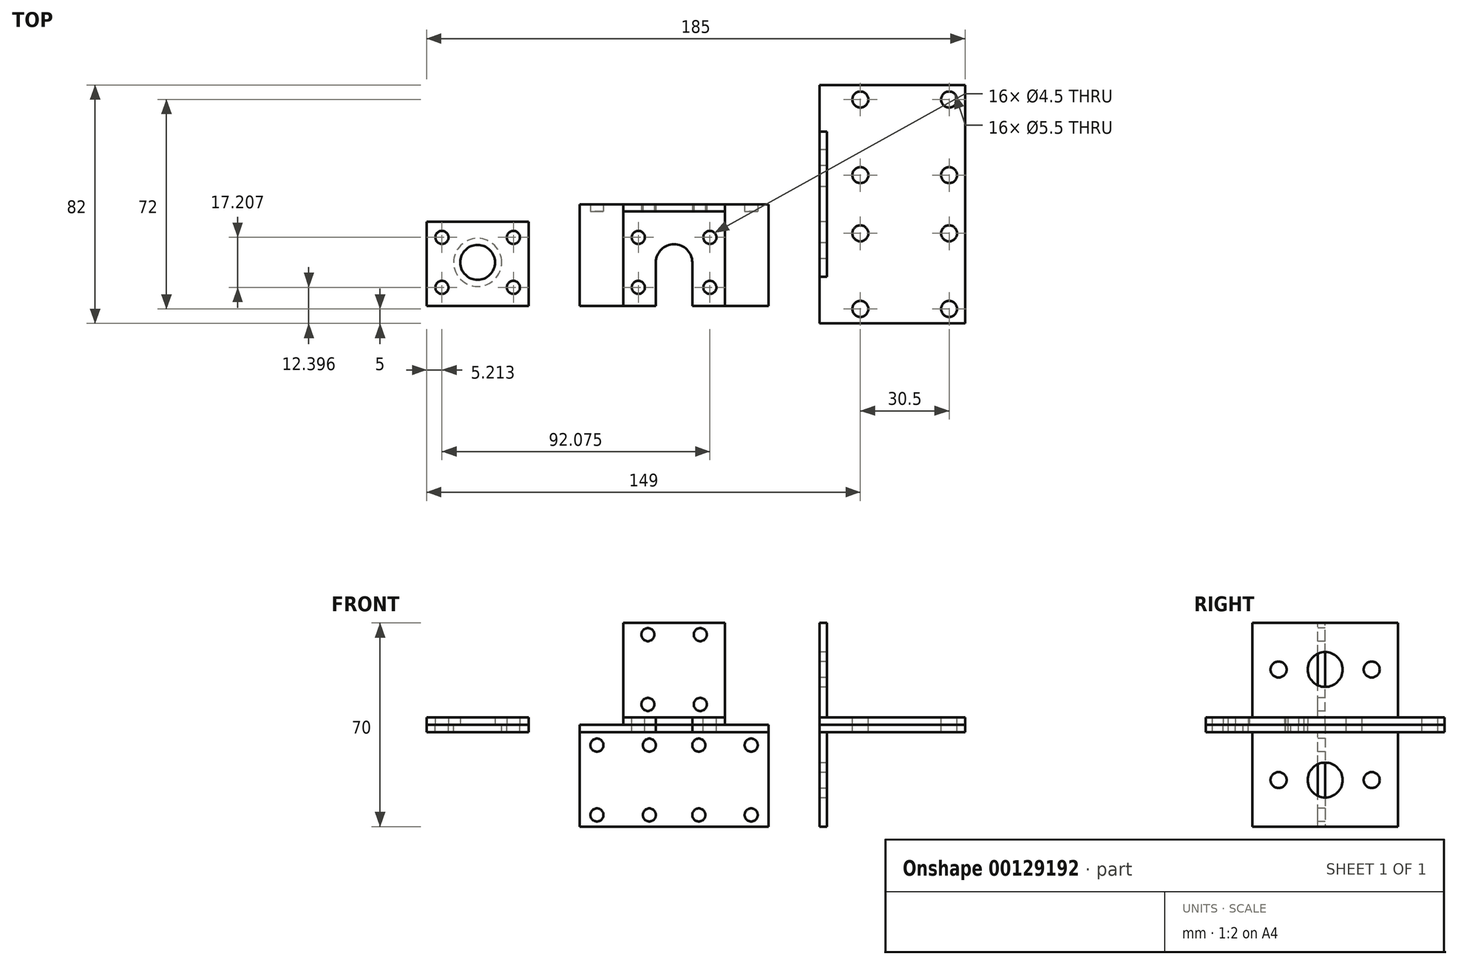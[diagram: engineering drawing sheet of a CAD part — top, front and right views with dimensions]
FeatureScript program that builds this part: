
annotation { "Feature Type Name" : "Feature", "Feature Type Description" : "" }
export const myFeature = defineFeature(function(context is Context, id is Id, definition is map)
    precondition{}
    {
        {
            var Q0;
            Q0=qCreatedBy(makeId("Right.planeOp"),FACE);
            cPlane(context, id + "F0", {"entities" : qUnion([Q0]), "cplaneType" : CPlaneType.OFFSET, "offset" : 50 * mm, "width" : 150 * mm, "height" : 150 * mm});
        }
        {
            var Q0;
            Q0=qCreatedBy(makeId("Right.planeOp"),FACE);
            var sketch = newSketch(context, id + "F1", { "sketchPlane" : qUnion([Q0])});
            skLineSegment(sketch, "E0.bottom", {"start": v(0, 0) * mm, "end": v(-35, 0) * mm});
            skLineSegment(sketch, "E0.top", {"start": v(0, 2.5) * mm, "end": v(-35, 2.5) * mm});
            skLineSegment(sketch, "E0.left", {"start": v(0, 0) * mm, "end": v(0, 2.5) * mm});
            skLineSegment(sketch, "E0.right", {"start": v(-35, 0) * mm, "end": v(-35, 2.5) * mm});
            skLineSegment(sketch, "E1.bottom", {"start": v(0, 2.5) * mm, "end": v(-2.5, 2.5) * mm});
            skLineSegment(sketch, "E1.top", {"start": v(0, 35) * mm, "end": v(-2.5, 35) * mm});
            skLineSegment(sketch, "E1.left", {"start": v(0, 2.5) * mm, "end": v(0, 35) * mm});
            skLineSegment(sketch, "E1.right", {"start": v(-2.5, 2.5) * mm, "end": v(-2.5, 35) * mm});
            skLineSegment(sketch, "E2.bottom", {"start": v(0, 0) * mm, "end": v(-2.5, 0) * mm});
            skLineSegment(sketch, "E2.right", {"start": v(-2.5, 0) * mm, "end": v(-2.5, 2.5) * mm});
            skSolve(sketch);
        }
        {
            var Q0;
            Q0=makeQuery(id+"F1.imprint","IMPRINT",FACE,{"disambiguationData":[TD([[makeQuery(id+"F1.imprint","IMPRINT",EDGE,{"derivedFrom":sQuery(id+"F1.wireOp",EDGE,"E0.bottom")}),-1.0]])]});
            var Q1;
            Q1=makeQuery(id+"F1.imprint","IMPRINT",FACE,{"disambiguationData":[TD([[makeQuery(id+"F1.imprint","IMPRINT",EDGE,{"derivedFrom":sQuery(id+"F1.wireOp",EDGE,"E2.bottom")}),-1.0]])]});
            extrude(context, id + "F2", {"entities" : qUnion([Q0, Q1]), "endBound" : BoundingType.SYMMETRIC, "depth" : 35 * mm});
        }
        {
            var Q0;
            Q0=makeQuery(id+"F1.imprint","IMPRINT",FACE,{"disambiguationData":[TD([[makeQuery(id+"F1.imprint","IMPRINT",EDGE,{"derivedFrom":sQuery(id+"F1.wireOp",EDGE,"E2.bottom")}),-1.0]])]});
            var Q1;
            Q1=makeQuery(id+"F1.imprint","IMPRINT",FACE,{"disambiguationData":[TD([[makeQuery(id+"F1.imprint","IMPRINT",EDGE,{"derivedFrom":sQuery(id+"F1.wireOp",EDGE,"E1.top")}),1.0]])]});
            extrude(context, id + "F3", {"entities" : qUnion([Q0, Q1]), "operationType" : NewBodyOperationType.ADD, "endBound" : BoundingType.SYMMETRIC, "depth" : 35 * mm});
        }
        {
            var Q0;
            Q0=qCreatedBy(makeId("Right.planeOp"),FACE);
            var sketch = newSketch(context, id + "F4", { "sketchPlane" : qUnion([Q0])});
            skLineSegment(sketch, "E3.bottom", {"start": v(0, -35) * mm, "end": v(-2.5, -35) * mm});
            skLineSegment(sketch, "E3.top", {"start": v(0, -2.5) * mm, "end": v(-2.5, -2.5) * mm});
            skLineSegment(sketch, "E3.left", {"start": v(0, -35) * mm, "end": v(0, -2.5) * mm});
            skLineSegment(sketch, "E3.right", {"start": v(-2.5, -35) * mm, "end": v(-2.5, -2.5) * mm});
            skLineSegment(sketch, "E4.bottom", {"start": v(0, 0) * mm, "end": v(-35, 0) * mm});
            skLineSegment(sketch, "E4.top", {"start": v(0, -2.5) * mm, "end": v(-35, -2.5) * mm});
            skLineSegment(sketch, "E4.left", {"start": v(0, 0) * mm, "end": v(0, -2.5) * mm});
            skLineSegment(sketch, "E4.right", {"start": v(-35, 0) * mm, "end": v(-35, -2.5) * mm});
            skLineSegment(sketch, "E5.bottom", {"start": v(-2.5, -2.5) * mm, "end": v(0, -2.5) * mm});
            skLineSegment(sketch, "E5.top", {"start": v(-2.5, 0) * mm, "end": v(0, 0) * mm});
            skLineSegment(sketch, "E5.left", {"start": v(-2.5, -2.5) * mm, "end": v(-2.5, 0) * mm});
            skLineSegment(sketch, "E5.right", {"start": v(0, -2.5) * mm, "end": v(0, 0) * mm});
            skSolve(sketch);
        }
        {
            var Q0;
            Q0=makeQuery(id+"F4.imprint","IMPRINT",FACE,{"disambiguationData":[TD([[makeQuery(id+"F4.imprint","IMPRINT",EDGE,{"derivedFrom":sQuery(id+"F4.wireOp",EDGE,"E4.bottom")}),1.0]])]});
            var Q1;
            Q1=makeQuery(id+"F4.imprint","IMPRINT",FACE,{"disambiguationData":[TD([[makeQuery(id+"F4.imprint","IMPRINT",EDGE,{"derivedFrom":sQuery(id+"F4.wireOp",EDGE,"E5.bottom")}),1.0]])]});
            extrude(context, id + "F5", {"entities" : qUnion([Q0, Q1]), "endBound" : BoundingType.SYMMETRIC, "depth" : 65 * mm});
        }
        {
            var Q0;
            Q0=makeQuery(id+"F4.imprint","IMPRINT",FACE,{"disambiguationData":[TD([[makeQuery(id+"F4.imprint","IMPRINT",EDGE,{"derivedFrom":sQuery(id+"F4.wireOp",EDGE,"E3.bottom")}),-1.0]])]});
            var Q1;
            Q1=makeQuery(id+"F4.imprint","IMPRINT",FACE,{"disambiguationData":[TD([[makeQuery(id+"F4.imprint","IMPRINT",EDGE,{"derivedFrom":sQuery(id+"F4.wireOp",EDGE,"E5.bottom")}),1.0]])]});
            extrude(context, id + "F6", {"entities" : qUnion([Q0, Q1]), "operationType" : NewBodyOperationType.ADD, "endBound" : BoundingType.SYMMETRIC, "depth" : 65 * mm});
        }
        {
            var Q0;
            Q0=qCreatedBy(makeId("Front.planeOp"),FACE);
            var sketch = newSketch(context, id + "F7", { "sketchPlane" : qUnion([Q0])});
            skLineSegment(sketch, "E6", {"start": v(78.4, 7) * mm, "end": v(-89.42, 7) * mm, "construction": true});
            skLineSegment(sketch, "E7", {"start": v(80.33, -7) * mm, "end": v(-90.65, -7) * mm, "construction": true});
            skLineSegment(sketch, "E8", {"start": v(62.65, 7) * mm, "end": v(62.65, 0) * mm, "construction": true});
            skLineSegment(sketch, "E9", {"start": v(62.65, 0) * mm, "end": v(62.65, -7) * mm, "construction": true});
            skCircle(sketch, "E10", {"center": v(-26.5, -7) * mm, "radius": 2.25 * mm});
            skCircle(sketch, "E11", {"center": v(-8.5, -7) * mm, "radius": 2.25 * mm});
            skCircle(sketch, "E12", {"center": v(8.5, -7) * mm, "radius": 2.25 * mm});
            skCircle(sketch, "E13", {"center": v(26.5, -7) * mm, "radius": 2.25 * mm});
            skLineSegment(sketch, "E14", {"start": v(-38.38, -31) * mm, "end": v(47.7, -31) * mm, "construction": true});
            skCircle(sketch, "E15", {"center": v(-26.5, -31) * mm, "radius": 2.25 * mm});
            skCircle(sketch, "E16", {"center": v(-8.5, -31) * mm, "radius": 2.25 * mm});
            skCircle(sketch, "E17", {"center": v(8.5, -31) * mm, "radius": 2.25 * mm});
            skCircle(sketch, "E18", {"center": v(26.5, -31) * mm, "radius": 2.25 * mm});
            skLineSegment(sketch, "E19", {"start": v(0, 52.5) * mm, "end": v(0, -66.42) * mm, "construction": true});
            skLineSegment(sketch, "E20", {"start": v(26.5, -5.99) * mm, "end": v(26.5, -56.02) * mm, "construction": true});
            skLineSegment(sketch, "E21", {"start": v(8.5, -5.9) * mm, "end": v(8.5, -56.8) * mm, "construction": true});
            skLineSegment(sketch, "E22", {"start": v(-8.5, -56.8) * mm, "end": v(-8.5, -6.69) * mm, "construction": true});
            skLineSegment(sketch, "E23", {"start": v(-26.5, -6.69) * mm, "end": v(-26.5, -58.57) * mm, "construction": true});
            skLineSegment(sketch, "E24", {"start": v(3.5, -5.72) * mm, "end": v(3.5, -57.57) * mm, "construction": true});
            skLineSegment(sketch, "E25", {"start": v(-3.5, -57.57) * mm, "end": v(-3.5, -6.02) * mm, "construction": true});
            skLineSegment(sketch, "E26", {"start": v(0, -48.24) * mm, "end": v(3.5, -48.24) * mm, "construction": true});
            skLineSegment(sketch, "E27", {"start": v(0, -48.24) * mm, "end": v(-3.5, -48.24) * mm, "construction": true});
            skLineSegment(sketch, "E28", {"start": v(8.5, -53.82) * mm, "end": v(3.5, -53.82) * mm, "construction": true});
            skLineSegment(sketch, "E29", {"start": v(-3.5, -54.17) * mm, "end": v(-8.5, -54.17) * mm, "construction": true});
            skLineSegment(sketch, "E30", {"start": v(46.98, 31) * mm, "end": v(-43.4, 31) * mm, "construction": true});
            skLineSegment(sketch, "E31", {"start": v(9, 3.25) * mm, "end": v(9, 53.28) * mm, "construction": true});
            skLineSegment(sketch, "E32", {"start": v(-9, 4.66) * mm, "end": v(-9, 53.81) * mm, "construction": true});
            skLineSegment(sketch, "E33", {"start": v(9, 48) * mm, "end": v(0, 48) * mm, "construction": true});
            skLineSegment(sketch, "E34", {"start": v(0, 48) * mm, "end": v(-9, 48) * mm, "construction": true});
            skCircle(sketch, "E35", {"center": v(9, 31) * mm, "radius": 2.25 * mm});
            skCircle(sketch, "E36", {"center": v(9, 7) * mm, "radius": 2.25 * mm});
            skCircle(sketch, "E37", {"center": v(-9, 7) * mm, "radius": 2.25 * mm});
            skCircle(sketch, "E38", {"center": v(-9, 31) * mm, "radius": 2.25 * mm});
            skSolve(sketch);
        }
        {
            var Q0;
            Q0=makeQuery(id+"F7.imprint","IMPRINT",FACE,{"disambiguationData":[TD([[makeQuery(id+"F7.imprint","IMPRINT",EDGE,{"derivedFrom":sQuery(id+"F7.wireOp",EDGE,"E35")}),1.0]])]});
            var Q1;
            Q1=makeQuery(id+"F7.imprint","IMPRINT",FACE,{"disambiguationData":[TD([[makeQuery(id+"F7.imprint","IMPRINT",EDGE,{"derivedFrom":sQuery(id+"F7.wireOp",EDGE,"E36")}),1.0]])]});
            var Q2;
            Q2=makeQuery(id+"F7.imprint","IMPRINT",FACE,{"disambiguationData":[TD([[makeQuery(id+"F7.imprint","IMPRINT",EDGE,{"derivedFrom":sQuery(id+"F7.wireOp",EDGE,"E37")}),1.0]])]});
            var Q3;
            Q3=makeQuery(id+"F7.imprint","IMPRINT",FACE,{"disambiguationData":[TD([[makeQuery(id+"F7.imprint","IMPRINT",EDGE,{"derivedFrom":sQuery(id+"F7.wireOp",EDGE,"E38")}),1.0]])]});
            extrude(context, id + "F8", {"entities" : qUnion([Q0, Q1, Q2, Q3]), "operationType" : NewBodyOperationType.REMOVE, "endBound" : BoundingType.SYMMETRIC, "oppositeDirection" : true, "depth" : 10 * mm});
        }
        {
            var Q0;
            Q0=makeQuery(id+"F7.imprint","IMPRINT",FACE,{"disambiguationData":[TD([[makeQuery(id+"F7.imprint","IMPRINT",EDGE,{"derivedFrom":sQuery(id+"F7.wireOp",EDGE,"E13")}),1.0]])]});
            var Q1;
            Q1=makeQuery(id+"F7.imprint","IMPRINT",FACE,{"disambiguationData":[TD([[makeQuery(id+"F7.imprint","IMPRINT",EDGE,{"derivedFrom":sQuery(id+"F7.wireOp",EDGE,"E12")}),1.0]])]});
            var Q2;
            Q2=makeQuery(id+"F7.imprint","IMPRINT",FACE,{"disambiguationData":[TD([[makeQuery(id+"F7.imprint","IMPRINT",EDGE,{"derivedFrom":sQuery(id+"F7.wireOp",EDGE,"E11")}),1.0]])]});
            var Q3;
            Q3=makeQuery(id+"F7.imprint","IMPRINT",FACE,{"disambiguationData":[TD([[makeQuery(id+"F7.imprint","IMPRINT",EDGE,{"derivedFrom":sQuery(id+"F7.wireOp",EDGE,"E10")}),1.0]])]});
            var Q4;
            Q4=makeQuery(id+"F7.imprint","IMPRINT",FACE,{"disambiguationData":[TD([[makeQuery(id+"F7.imprint","IMPRINT",EDGE,{"derivedFrom":sQuery(id+"F7.wireOp",EDGE,"E15")}),1.0]])]});
            var Q5;
            Q5=makeQuery(id+"F7.imprint","IMPRINT",FACE,{"disambiguationData":[TD([[makeQuery(id+"F7.imprint","IMPRINT",EDGE,{"derivedFrom":sQuery(id+"F7.wireOp",EDGE,"E16")}),1.0]])]});
            var Q6;
            Q6=makeQuery(id+"F7.imprint","IMPRINT",FACE,{"disambiguationData":[TD([[makeQuery(id+"F7.imprint","IMPRINT",EDGE,{"derivedFrom":sQuery(id+"F7.wireOp",EDGE,"E17")}),1.0]])]});
            var Q7;
            Q7=makeQuery(id+"F7.imprint","IMPRINT",FACE,{"disambiguationData":[TD([[makeQuery(id+"F7.imprint","IMPRINT",EDGE,{"derivedFrom":sQuery(id+"F7.wireOp",EDGE,"E18")}),1.0]])]});
            extrude(context, id + "F9", {"entities" : qUnion([Q0, Q1, Q2, Q3, Q4, Q5, Q6, Q7]), "operationType" : NewBodyOperationType.REMOVE, "endBound" : BoundingType.SYMMETRIC, "oppositeDirection" : true, "depth" : 10 * mm});
        }
        {
            var Q0;
            Q0=qCreatedBy(makeId("Top.planeOp"),FACE);
            var sketch = newSketch(context, id + "F10", { "sketchPlane" : qUnion([Q0])});
            skLineSegment(sketch, "E39.bottom", {"start": v(-85, -6) * mm, "end": v(-50, -6) * mm});
            skLineSegment(sketch, "E39.top", {"start": v(-85, -35) * mm, "end": v(-50, -35) * mm});
            skLineSegment(sketch, "E39.left", {"start": v(-85, -35) * mm, "end": v(-85, -6) * mm});
            skLineSegment(sketch, "E39.right", {"start": v(-50, -35) * mm, "end": v(-50, -6) * mm});
            skLineSegment(sketch, "E40", {"start": v(-85, -20) * mm, "end": v(-67.5, -20) * mm, "construction": true});
            skLineSegment(sketch, "E41", {"start": v(-67.5, -20) * mm, "end": v(-50, -20) * mm, "construction": true});
            skLineSegment(sketch, "E42", {"start": v(-67.5, -35) * mm, "end": v(-67.5, -20) * mm, "construction": true});
            skCircle(sketch, "E43", {"center": v(-67.5, -20) * mm, "radius": 8.25 * mm});
            skCircle(sketch, "E44", {"center": v(-79.79, -28.6) * mm, "radius": 2.25 * mm});
            skLineSegment(sketch, "E45", {"start": v(-67.5, -20) * mm, "end": v(-55.21, -11.4) * mm, "construction": true});
            skLineSegment(sketch, "E46", {"start": v(-79.79, -28.6) * mm, "end": v(-67.5, -20) * mm});
            skCircle(sketch, "E47", {"center": v(-55.21, -11.4) * mm, "radius": 2.25 * mm});
            skCircle(sketch, "E48", {"center": v(-79.79, -11.4) * mm, "radius": 2.25 * mm});
            skLineSegment(sketch, "E49", {"start": v(-67.5, -20) * mm, "end": v(-79.79, -11.4) * mm, "construction": true});
            skCircle(sketch, "E50", {"center": v(-55.21, -28.6) * mm, "radius": 2.25 * mm});
            skLineSegment(sketch, "E51", {"start": v(-67.5, -20) * mm, "end": v(-55.21, -28.6) * mm, "construction": true});
            skCircle(sketch, "E52", {"center": v(-67.5, -20) * mm, "radius": 6 * mm});
            skLineSegment(sketch, "E53", {"start": v(-37.49, -20) * mm, "end": v(-99.92, -20) * mm, "construction": true});
            skSolve(sketch);
        }
        {
            var Q0;
            Q0=qCreatedBy(makeId("Top.planeOp"),FACE);
            var sketch = newSketch(context, id + "F11", { "sketchPlane" : qUnion([Q0])});
            skLineSegment(sketch, "E54", {"start": v(0, 16.43) * mm, "end": v(0, -56.43) * mm, "construction": true});
            skLineSegment(sketch, "E55", {"start": v(-39.4, -20) * mm, "end": v(51.73, -20) * mm, "construction": true});
            skPoint(sketch, "E55.endSnap0", {"position": v(0, -20) * mm});
            skCircle(sketch, "E56", {"center": v(0, -20) * mm, "radius": 6.25 * mm});
            skLineSegment(sketch, "E57", {"start": v(-6.25, -20) * mm, "end": v(-6.25, -44.93) * mm});
            skLineSegment(sketch, "E58", {"start": v(-6.25, -44.93) * mm, "end": v(6.25, -44.93) * mm});
            skLineSegment(sketch, "E59", {"start": v(6.25, -44.93) * mm, "end": v(6.25, -20) * mm});
            skLineSegment(sketch, "E60", {"start": v(0, -20) * mm, "end": v(12.29, -11.4) * mm, "construction": true});
            skLineSegment(sketch, "E61", {"start": v(0, -20) * mm, "end": v(-12.29, -11.4) * mm, "construction": true});
            skLineSegment(sketch, "E62", {"start": v(0, -20) * mm, "end": v(-12.29, -28.6) * mm, "construction": true});
            skLineSegment(sketch, "E63", {"start": v(0, -20) * mm, "end": v(12.29, -28.6) * mm, "construction": true});
            skCircle(sketch, "E64", {"center": v(-12.29, -11.4) * mm, "radius": 2.25 * mm});
            skCircle(sketch, "E65", {"center": v(12.29, -11.4) * mm, "radius": 2.25 * mm});
            skCircle(sketch, "E66", {"center": v(12.29, -28.6) * mm, "radius": 2.25 * mm});
            skCircle(sketch, "E67", {"center": v(-12.29, -28.6) * mm, "radius": 2.25 * mm});
            skSolve(sketch);
        }
        {
            var Q0;
            Q0=makeQuery(id+"F11.imprint","IMPRINT",FACE,{"disambiguationData":[TD([[makeQuery(id+"F11.imprint","IMPRINT",EDGE,{"derivedFrom":sQuery(id+"F11.wireOp",EDGE,"E56")}),1.0]])]});
            var Q1;
            {var subQ0=sQuery(id+"F11.wireOp",EDGE,"E57");Q1=makeQuery(id+"F11.imprint","IMPRINT",FACE,{"disambiguationData":[TD([[makeQuery(id+"F11.imprint","IMPRINT",EDGE,{"derivedFrom":subQ0}),1.0]])]});}
            var Q2;
            Q2=makeQuery(id+"F11.imprint","IMPRINT",FACE,{"disambiguationData":[TD([[makeQuery(id+"F11.imprint","IMPRINT",EDGE,{"derivedFrom":sQuery(id+"F11.wireOp",EDGE,"E64")}),1.0]])]});
            var Q3;
            Q3=makeQuery(id+"F11.imprint","IMPRINT",FACE,{"disambiguationData":[TD([[makeQuery(id+"F11.imprint","IMPRINT",EDGE,{"derivedFrom":sQuery(id+"F11.wireOp",EDGE,"E65")}),1.0]])]});
            var Q4;
            Q4=makeQuery(id+"F11.imprint","IMPRINT",FACE,{"disambiguationData":[TD([[makeQuery(id+"F11.imprint","IMPRINT",EDGE,{"derivedFrom":sQuery(id+"F11.wireOp",EDGE,"E66")}),1.0]])]});
            var Q5;
            Q5=makeQuery(id+"F11.imprint","IMPRINT",FACE,{"disambiguationData":[TD([[makeQuery(id+"F11.imprint","IMPRINT",EDGE,{"derivedFrom":sQuery(id+"F11.wireOp",EDGE,"E67")}),1.0]])]});
            extrude(context, id + "F12", {"entities" : qUnion([Q0, Q1, Q2, Q3, Q4, Q5]), "operationType" : NewBodyOperationType.REMOVE, "endBound" : BoundingType.SYMMETRIC, "oppositeDirection" : true, "depth" : 10 * mm});
        }
        {
            var Q0;
            Q0=makeQuery(id+"F10.imprint","IMPRINT",FACE,{"disambiguationData":[TD([[makeQuery(id+"F10.imprint","IMPRINT",EDGE,{"derivedFrom":sQuery(id+"F10.wireOp",EDGE,"E39.bottom")}),-1.0]])]});
            extrude(context, id + "F13", {"entities" : qUnion([Q0]), "oppositeDirection" : true, "depth" : 2.5 * mm});
        }
        {
            var Q0;
            Q0=makeQuery(id+"F10.imprint","IMPRINT",FACE,{"disambiguationData":[TD([[makeQuery(id+"F10.imprint","IMPRINT",EDGE,{"derivedFrom":sQuery(id+"F10.wireOp",EDGE,"E39.bottom")}),-1.0]])]});
            var Q1;
            Q1=makeQuery(id+"F10.imprint","IMPRINT",FACE,{"disambiguationData":[TD([[makeQuery(id+"F10.imprint","IMPRINT",EDGE,{"derivedFrom":sQuery(id+"F10.wireOp",EDGE,"E43")}),1.0]])]});
            extrude(context, id + "F14", {"entities" : qUnion([Q0, Q1]), "depth" : 2.5 * mm});
        }
        {
            var Q0;
            Q0=qCreatedBy(makeId("Front.planeOp"),FACE);
            var sketch = newSketch(context, id + "F15", { "sketchPlane" : qUnion([Q0])});
            skLineSegment(sketch, "E68", {"start": v(50, 72.04) * mm, "end": v(50, -62.88) * mm, "construction": true});
            skLineSegment(sketch, "E69.bottom", {"start": v(50, 0) * mm, "end": v(100, 0) * mm});
            skLineSegment(sketch, "E69.top", {"start": v(50, -2.5) * mm, "end": v(100, -2.5) * mm});
            skLineSegment(sketch, "E69.left", {"start": v(50, 0) * mm, "end": v(50, -2.5) * mm});
            skLineSegment(sketch, "E69.right", {"start": v(100, 0) * mm, "end": v(100, -2.5) * mm});
            skLineSegment(sketch, "E70.bottom", {"start": v(50, -2.5) * mm, "end": v(52.5, -2.5) * mm});
            skLineSegment(sketch, "E70.top", {"start": v(50, -35) * mm, "end": v(52.5, -35) * mm});
            skLineSegment(sketch, "E70.left", {"start": v(50, -2.5) * mm, "end": v(50, -35) * mm});
            skLineSegment(sketch, "E70.right", {"start": v(52.5, -2.5) * mm, "end": v(52.5, -35) * mm});
            skLineSegment(sketch, "E71.bottom", {"start": v(100, 2.5) * mm, "end": v(50, 2.5) * mm});
            skLineSegment(sketch, "E71.top", {"start": v(100, 0) * mm, "end": v(50, 0) * mm});
            skLineSegment(sketch, "E71.left", {"start": v(100, 2.5) * mm, "end": v(100, 0) * mm});
            skLineSegment(sketch, "E71.right", {"start": v(50, 2.5) * mm, "end": v(50, 0) * mm});
            skLineSegment(sketch, "E72.bottom", {"start": v(52.5, 2.5) * mm, "end": v(50, 2.5) * mm});
            skLineSegment(sketch, "E72.top", {"start": v(52.5, 35) * mm, "end": v(50, 35) * mm});
            skLineSegment(sketch, "E72.left", {"start": v(52.5, 2.5) * mm, "end": v(52.5, 35) * mm});
            skLineSegment(sketch, "E72.right", {"start": v(50, 2.5) * mm, "end": v(50, 35) * mm});
            skLineSegment(sketch, "E73.bottom", {"start": v(50, 2.5) * mm, "end": v(52.5, 2.5) * mm});
            skLineSegment(sketch, "E73.top", {"start": v(50, 0) * mm, "end": v(52.5, 0) * mm});
            skLineSegment(sketch, "E73.right", {"start": v(52.5, 2.5) * mm, "end": v(52.5, 0) * mm});
            skLineSegment(sketch, "E74.right", {"start": v(52.5, 0) * mm, "end": v(52.5, -2.5) * mm});
            skSolve(sketch);
        }
        {
            var Q0;
            Q0=makeQuery(id+"F15.imprint","IMPRINT",FACE,{"disambiguationData":[TD([[makeQuery(id+"F15.imprint","IMPRINT",EDGE,{"derivedFrom":sQuery(id+"F15.wireOp",EDGE,"E70.top")}),1.0]])]});
            var Q1;
            Q1=makeQuery(id+"F15.imprint","IMPRINT",FACE,{"disambiguationData":[TD([[makeQuery(id+"F15.imprint","IMPRINT",EDGE,{"derivedFrom":sQuery(id+"F15.wireOp",EDGE,"E73.top")}),-1.0]])]});
            extrude(context, id + "F16", {"entities" : qUnion([Q0, Q1]), "endBound" : BoundingType.SYMMETRIC, "depth" : 50 * mm});
        }
        {
            var Q0;
            Q0=makeQuery(id+"F15.imprint","IMPRINT",FACE,{"disambiguationData":[TD([[makeQuery(id+"F15.imprint","IMPRINT",EDGE,{"derivedFrom":sQuery(id+"F15.wireOp",EDGE,"E73.top")}),-1.0]])]});
            var Q1;
            Q1=makeQuery(id+"F15.imprint","IMPRINT",FACE,{"disambiguationData":[TD([[makeQuery(id+"F15.imprint","IMPRINT",EDGE,{"derivedFrom":sQuery(id+"F15.wireOp",EDGE,"E69.top")}),1.0]])]});
            extrude(context, id + "F17", {"entities" : qUnion([Q0, Q1]), "operationType" : NewBodyOperationType.ADD, "endBound" : BoundingType.SYMMETRIC, "depth" : 82 * mm});
        }
        {
            var Q0;
            Q0=makeQuery(id+"F15.imprint","IMPRINT",FACE,{"disambiguationData":[TD([[makeQuery(id+"F15.imprint","IMPRINT",EDGE,{"derivedFrom":sQuery(id+"F15.wireOp",EDGE,"E71.bottom")}),1.0]])]});
            var Q1;
            Q1=makeQuery(id+"F15.imprint","IMPRINT",FACE,{"disambiguationData":[TD([[makeQuery(id+"F15.imprint","IMPRINT",EDGE,{"derivedFrom":sQuery(id+"F15.wireOp",EDGE,"E73.bottom")}),-1.0]])]});
            extrude(context, id + "F18", {"entities" : qUnion([Q0, Q1]), "endBound" : BoundingType.SYMMETRIC, "depth" : 82 * mm});
        }
        {
            var Q0;
            Q0=makeQuery(id+"F15.imprint","IMPRINT",FACE,{"disambiguationData":[TD([[makeQuery(id+"F15.imprint","IMPRINT",EDGE,{"derivedFrom":sQuery(id+"F15.wireOp",EDGE,"E72.top")}),1.0]])]});
            var Q1;
            Q1=makeQuery(id+"F15.imprint","IMPRINT",FACE,{"disambiguationData":[TD([[makeQuery(id+"F15.imprint","IMPRINT",EDGE,{"derivedFrom":sQuery(id+"F15.wireOp",EDGE,"E73.bottom")}),-1.0]])]});
            extrude(context, id + "F19", {"entities" : qUnion([Q0, Q1]), "operationType" : NewBodyOperationType.ADD, "endBound" : BoundingType.SYMMETRIC, "depth" : 50 * mm});
        }
        {
            var Q0;
            Q0=qCreatedBy(id+"F0.planeOp",FACE);
            var sketch = newSketch(context, id + "F20", { "sketchPlane" : qUnion([Q0])});
            skLineSegment(sketch, "E75", {"start": v(0, 46.98) * mm, "end": v(0, -48.24) * mm, "construction": true});
            skLineSegment(sketch, "E76", {"start": v(9.78, -19) * mm, "end": v(-53.56, -19) * mm, "construction": true});
            skLineSegment(sketch, "E77", {"start": v(11.82, 19) * mm, "end": v(-55.78, 19) * mm, "construction": true});
            skLineSegment(sketch, "E78", {"start": v(16, 41) * mm, "end": v(16, -46) * mm, "construction": true});
            skLineSegment(sketch, "E79", {"start": v(-16, 39.47) * mm, "end": v(-16, -46.35) * mm, "construction": true});
            skCircle(sketch, "E80", {"center": v(16, -19) * mm, "radius": 2.75 * mm});
            skCircle(sketch, "E81", {"center": v(-16, -19) * mm, "radius": 2.75 * mm});
            skCircle(sketch, "E82", {"center": v(16, 19) * mm, "radius": 2.75 * mm});
            skCircle(sketch, "E83", {"center": v(0, 19) * mm, "radius": 6 * mm});
            skCircle(sketch, "E84", {"center": v(0, -19) * mm, "radius": 6 * mm});
            skCircle(sketch, "E85", {"center": v(-16, 19) * mm, "radius": 2.75 * mm});
            skSolve(sketch);
        }
        {
            var Q0;
            Q0=makeQuery(id+"F20.imprint","IMPRINT",FACE,{"disambiguationData":[TD([[makeQuery(id+"F20.imprint","IMPRINT",EDGE,{"derivedFrom":sQuery(id+"F20.wireOp",EDGE,"E80")}),1.0]])]});
            var Q1;
            Q1=makeQuery(id+"F20.imprint","IMPRINT",FACE,{"disambiguationData":[TD([[makeQuery(id+"F20.imprint","IMPRINT",EDGE,{"derivedFrom":sQuery(id+"F20.wireOp",EDGE,"E84")}),1.0]])]});
            var Q2;
            Q2=makeQuery(id+"F20.imprint","IMPRINT",FACE,{"disambiguationData":[TD([[makeQuery(id+"F20.imprint","IMPRINT",EDGE,{"derivedFrom":sQuery(id+"F20.wireOp",EDGE,"E81")}),1.0]])]});
            extrude(context, id + "F21", {"entities" : qUnion([Q0, Q1, Q2]), "operationType" : NewBodyOperationType.REMOVE, "endBound" : BoundingType.SYMMETRIC, "oppositeDirection" : true, "depth" : 5 * mm});
        }
        {
            var Q0;
            Q0=makeQuery(id+"F20.imprint","IMPRINT",FACE,{"disambiguationData":[TD([[makeQuery(id+"F20.imprint","IMPRINT",EDGE,{"derivedFrom":sQuery(id+"F20.wireOp",EDGE,"E85")}),1.0]])]});
            var Q1;
            Q1=makeQuery(id+"F20.imprint","IMPRINT",FACE,{"disambiguationData":[TD([[makeQuery(id+"F20.imprint","IMPRINT",EDGE,{"derivedFrom":sQuery(id+"F20.wireOp",EDGE,"E83")}),1.0]])]});
            var Q2;
            Q2=makeQuery(id+"F20.imprint","IMPRINT",FACE,{"disambiguationData":[TD([[makeQuery(id+"F20.imprint","IMPRINT",EDGE,{"derivedFrom":sQuery(id+"F20.wireOp",EDGE,"E82")}),1.0]])]});
            extrude(context, id + "F22", {"entities" : qUnion([Q0, Q1, Q2]), "operationType" : NewBodyOperationType.REMOVE, "endBound" : BoundingType.SYMMETRIC, "depth" : 10 * mm});
        }
        {
            var Q0;
            Q0=qCreatedBy(makeId("Top.planeOp"),FACE);
            var sketch = newSketch(context, id + "F23", { "sketchPlane" : qUnion([Q0])});
            skLineSegment(sketch, "E86", {"start": v(94.5, 47) * mm, "end": v(94.5, -47) * mm, "construction": true});
            skLineSegment(sketch, "E87", {"start": v(40, -36) * mm, "end": v(130, -36) * mm, "construction": true});
            skLineSegment(sketch, "E88", {"start": v(130, -10) * mm, "end": v(40.78, -10) * mm, "construction": true});
            skCircle(sketch, "E89", {"center": v(64, -10) * mm, "radius": 2.75 * mm});
            skCircle(sketch, "E90", {"center": v(94.5, -10) * mm, "radius": 2.75 * mm});
            skCircle(sketch, "E91", {"center": v(94.5, -36) * mm, "radius": 2.75 * mm});
            skCircle(sketch, "E92", {"center": v(64, -36) * mm, "radius": 2.75 * mm});
            skLineSegment(sketch, "E93", {"start": v(40.78, 10) * mm, "end": v(130, 10) * mm, "construction": true});
            skLineSegment(sketch, "E94", {"start": v(40.78, 36) * mm, "end": v(130, 36) * mm, "construction": true});
            skCircle(sketch, "E95", {"center": v(64, 10) * mm, "radius": 2.75 * mm});
            skCircle(sketch, "E96", {"center": v(94.5, 10) * mm, "radius": 2.75 * mm});
            skCircle(sketch, "E97", {"center": v(94.5, 36) * mm, "radius": 2.75 * mm});
            skCircle(sketch, "E98", {"center": v(64, 36) * mm, "radius": 2.75 * mm});
            skLineSegment(sketch, "E99", {"start": v(64, 47) * mm, "end": v(64, -47) * mm, "construction": true});
            skSolve(sketch);
        }
        {
            var Q0;
            Q0=makeQuery(id+"F23.imprint","IMPRINT",FACE,{"disambiguationData":[TD([[makeQuery(id+"F23.imprint","IMPRINT",EDGE,{"derivedFrom":sQuery(id+"F23.wireOp",EDGE,"E89")}),1.0]])]});
            var Q1;
            Q1=makeQuery(id+"F23.imprint","IMPRINT",FACE,{"disambiguationData":[TD([[makeQuery(id+"F23.imprint","IMPRINT",EDGE,{"derivedFrom":sQuery(id+"F23.wireOp",EDGE,"E90")}),1.0]])]});
            var Q2;
            Q2=makeQuery(id+"F23.imprint","IMPRINT",FACE,{"disambiguationData":[TD([[makeQuery(id+"F23.imprint","IMPRINT",EDGE,{"derivedFrom":sQuery(id+"F23.wireOp",EDGE,"E91")}),1.0]])]});
            var Q3;
            Q3=makeQuery(id+"F23.imprint","IMPRINT",FACE,{"disambiguationData":[TD([[makeQuery(id+"F23.imprint","IMPRINT",EDGE,{"derivedFrom":sQuery(id+"F23.wireOp",EDGE,"E92")}),1.0]])]});
            var Q4;
            Q4=makeQuery(id+"F23.imprint","IMPRINT",FACE,{"disambiguationData":[TD([[makeQuery(id+"F23.imprint","IMPRINT",EDGE,{"derivedFrom":sQuery(id+"F23.wireOp",EDGE,"E98")}),1.0]])]});
            var Q5;
            Q5=makeQuery(id+"F23.imprint","IMPRINT",FACE,{"disambiguationData":[TD([[makeQuery(id+"F23.imprint","IMPRINT",EDGE,{"derivedFrom":sQuery(id+"F23.wireOp",EDGE,"E97")}),1.0]])]});
            var Q6;
            Q6=makeQuery(id+"F23.imprint","IMPRINT",FACE,{"disambiguationData":[TD([[makeQuery(id+"F23.imprint","IMPRINT",EDGE,{"derivedFrom":sQuery(id+"F23.wireOp",EDGE,"E95")}),1.0]])]});
            var Q7;
            Q7=makeQuery(id+"F23.imprint","IMPRINT",FACE,{"disambiguationData":[TD([[makeQuery(id+"F23.imprint","IMPRINT",EDGE,{"derivedFrom":sQuery(id+"F23.wireOp",EDGE,"E96")}),1.0]])]});
            extrude(context, id + "F24", {"entities" : qUnion([Q0, Q1, Q2, Q3, Q4, Q5, Q6, Q7]), "operationType" : NewBodyOperationType.REMOVE, "endBound" : BoundingType.SYMMETRIC, "oppositeDirection" : true, "depth" : 10 * mm});
        }
    });
